# Revit family: DBLTD_Kwickscreen_PrvcyScrn_Shield
name_source: partatom
category: Furniture
units: mm (PartAtom-declared; Revit-internal decimal feet)

## family parameters
Always vertical = Yes
Cut with Voids When Loaded = No
OmniClass Number = 23.40.20.00
OmniClass Title = General Furniture and Specialties
Room Calculation Point = No
Shared = Yes
Work Plane-Based = No

## types (4) — shared parameters
Assembly Code = E2020200
AssetType = Movable
Category = Pr_40_30_20_65:Privacy screens
DimensionsHeight = 1400
DimensionsPlanSize = 1100 mm x 850 mm
DurationUnit = Years
ExpectedLife = 10
Features = Freestanding chair partitions
Finish = Silver anodized Aluminium
FramesColour = Silver
IfcExportAs = IfcFurnitureTypeEnum
IfcExportType = Screen
IsBuiltIn = No
Keynote = Pr_40_30_20_65
Manufacturer = KwickScreen
ManufacturerName = KwickScreen
ManufacturerURL = https://kwickscreen.com
Material = Aluminium
NBSDescription = Freestanding Screens
NBSReference = 45-35-25/320
Name = PrivacyScreens_Shield_KwickScreen
NominalDepth = 580 mm  [stored 1.90289 ft]
NominalHeight = 1400 mm  [stored 4.59318 ft]
NominalLength = 580 mm  [stored 1.90289 ft]
NominalWidth = 580 mm  [stored 1.90289 ft]
ProductInformation = https://kwickscreen.com
ReplacementCost = 0
Shape = Rectangular
URL = https://kwickscreen.com
Uniclass2015Code = Pr_40_30_20_65
Uniclass2015Title = Privacy screens
Uniclass2015Version = Products v1.9
Version = 1
WarrantyDurationUnit = Years
zero-valued in all types: Cost, Default Elevation

## per-type parameters (varying)
| type | Description | DoubleScreen | Model | ModelNumber | ModelReference | ScreenType | Size | Type Comments |
| Screen with 1 Panel Right | Screen with 1 Panel Right | No | Shield Single | Shield Single | Screen with 1 Panel Right | DBLTD_Kwickscreen_PrvcyScrn_Shield : Single Screen Right | L 580mm x  W 580mm x  H 1400mm | Screen with 1 Panel Right |
| Screen with 2 Panels Right | Screen with 2 Panel Right | Yes | Shield Dual | Shield Dual | Screen with 2 Panel Right | DBLTD_Kwickscreen_PrvcyScrn_Shield : Double Screen Right | L 580mm x  W 600mm x  H 1400mm | Screen with 2 Panel Right |
| Screen with 2 Panels Left | Screen with 2 Panel Left | Yes | Shield Dual | Shield Dual | Screen with 2 Panel Left | DBLTD_Kwickscreen_PrvcyScrn_Shield : Double Screen Left | L 580mm x  W 600mm x  H 1400mm | Screen with 2 Panel Left |
| Screen with 1 Panel Left | Screen with 1 Panel Left | No | Shield Single | Shield Single | Screen with 1 Panel Left | DBLTD_Kwickscreen_PrvcyScrn_Shield : Single Screen Right | L 580mm x  W 580mm x  H 1400mm | Screen with 1 Panel Left |

note: [stored X ft] marks values corroborated as IEEE doubles in the binary element streams (Revit-internal decimal feet)

## geometry (parser evidence)
native form markers: Sweep x4
no freeform markers — native parametric forms only
